# Revit family: Toilet-Elongated-Top_Spud-American_Standard-Priolo_FloWise-369X_Series
name_source: partatom
category: Plumbing Fixtures
revit_build: Autodesk Revit 2015 (Build: 20140606_1530(x64)
units: mm (PartAtom-declared; Revit-internal decimal feet)

## types (2) — shared parameters
Assembly Code = D2010110
Bowl Shape = Elongated
CW Connection = Yes
CWFU = 10
Cold Water Connection Diameter = 1"
Cold Water Connection Height = 26 1/2"
Cold Water Connection Radius = 1/2"
Cold Water Connection Width = 4 3/4"
Default Elevation = 0"
Description = Priolo 1.1-1.6 gpf EverClean Universal Flushometer Toilet
Finish = Vitreous China-American Standard-020-White
Flush Rate = 1.1 gpf (4.2 Lpf) to 1.6 gpf  (6.0 Lpf)
HW Connection = No
Height = 15"
Installation Type = Floor Mounted
Length = 29 5/8"
Manufacturer = American Standard
Material = Vitreous China-American Standard-020-White
Price = Prices may vary. Please consult Manufacturer Representative for most up-to-date price list.
Product Documentation Link = https://www.americanstandard-us.com
Product Page URL = https://www.americanstandard-us.com
Revised Date = 03/20/2020
URL = http://www.americanstandard-us.com
Vent Connection = No
WFU = 10
Waste Connection = Yes
Waste Connection Diameter = 2 1/8"
Waste Connection Radius = 1 1/16"
Width = 14"
zero-valued in all types: HWFU

## per-type parameters (varying)
| type | Bowl Rim | Slotted rim for bedpan holding. |
| 3691.001.020 | No | Yes |
| 3690.001.020 | Yes | No |

note: column(s) folded — value = type name in every type: Model

## geometry (parser evidence)
native form markers: Sweep x4
no freeform markers — native parametric forms only
